# Revit family: Shower_Head-GROHE-Cosmopolitan_100-27591_Series
name_source: partatom
category: Plumbing Fixtures
revit_build: Autodesk Revit 2014 (Build: 20130308_1515(x64)
units: mm (PartAtom-declared; Revit-internal decimal feet)

## types (2) — shared parameters
Assembly Code = D2010700
CW Connection = Yes
CWFU = 2
Connection Diameter = 1/2"
Default Elevation = 0"
Description = New Tempesta Cosmopolitan 100.
Flow Rate = 2.5 gpm at 80 psi (9.5 L/min)
HW Connection = Yes
HWFU = 3
Height = 3 5/16"
Manufacturer = GROHE
Price = Prices may vary. Please consult Manufacturer Representative for most up-to-date price list.
Product Page URL = http://www.grohe.com
URL = http://www.grohe.com
Vent Connection = No
WFU = 4
Warranty Information = Limited Lifetime Warranty
Waste Connection = No
Width = 3 15/16"

## per-type parameters (varying)
| type | Finish | Material |
| 27591000 | Metal-Grohe-000-Chrome | Metal-Grohe-000-Chrome |
| 27591EN0 | Metal-Grohe-EN0-Brushed Nickel | Metal-Grohe-EN0-Brushed Nickel |

note: column(s) folded — value = type name in every type: Model

## geometry (parser evidence)
native form markers: Sweep x1
no freeform markers — native parametric forms only
